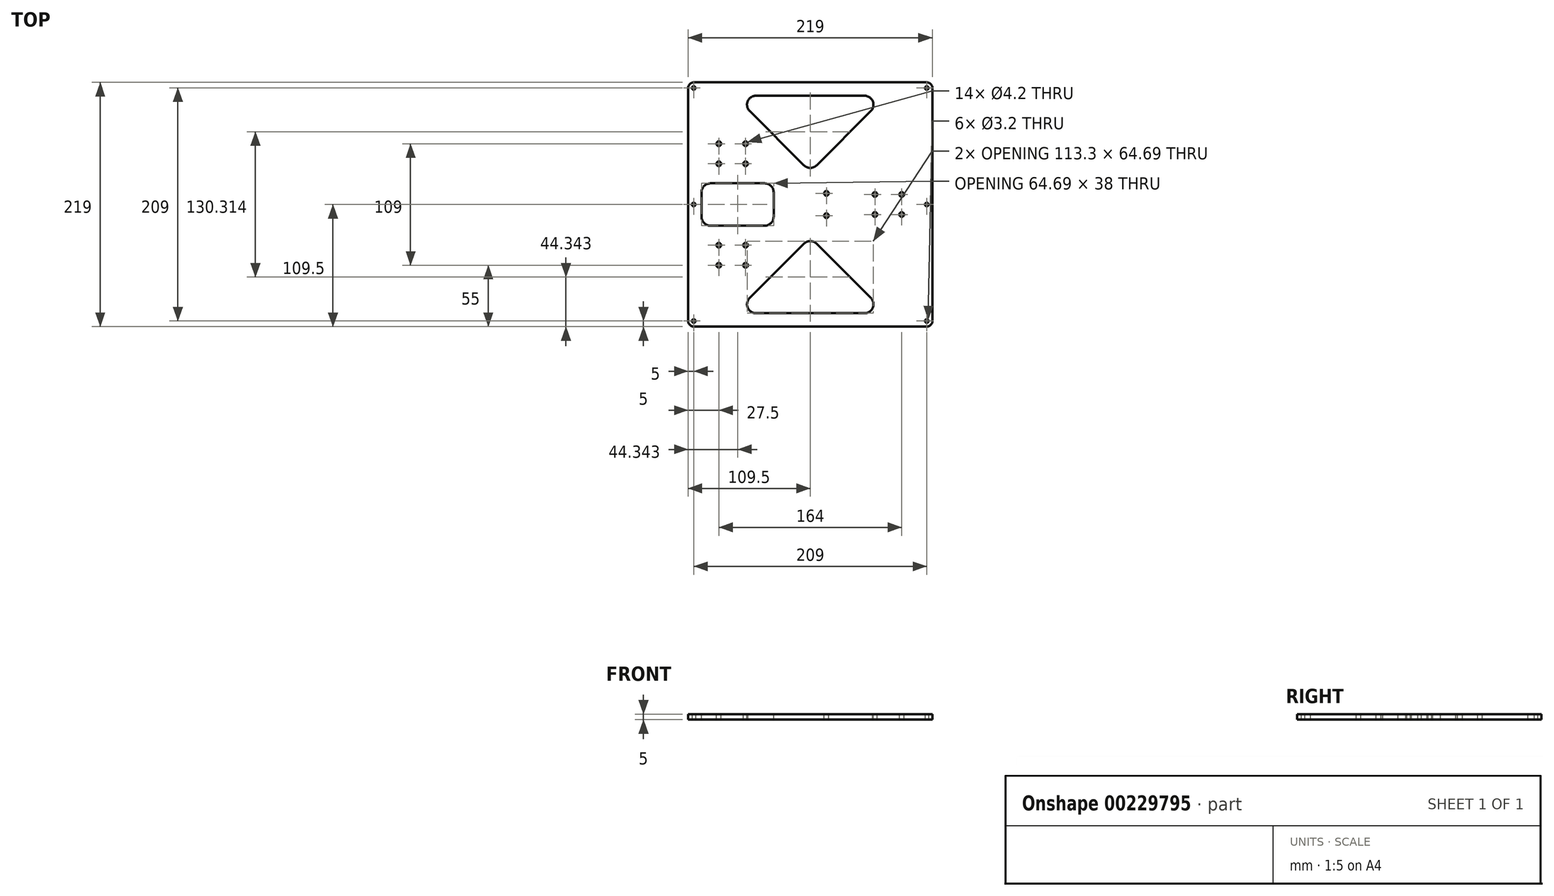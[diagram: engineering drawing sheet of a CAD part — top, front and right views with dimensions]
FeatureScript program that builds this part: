
annotation { "Feature Type Name" : "Feature", "Feature Type Description" : "" }
export const myFeature = defineFeature(function(context is Context, id is Id, definition is map)
    precondition{}
    {
        {
            var Q0;
            Q0=qCreatedBy(makeId("Top.planeOp"),FACE);
            var sketch = newSketch(context, id + "F0", { "sketchPlane" : qUnion([Q0])});
            skLineSegment(sketch, "E0.bottom", {"start": v(109.5, 109.5) * mm, "end": v(-109.5, 109.5) * mm});
            skLineSegment(sketch, "E0.top", {"start": v(109.5, -109.5) * mm, "end": v(-109.5, -109.5) * mm});
            skLineSegment(sketch, "E0.left", {"start": v(109.5, 109.5) * mm, "end": v(109.5, -109.5) * mm});
            skLineSegment(sketch, "E0.right", {"start": v(-109.5, 109.5) * mm, "end": v(-109.5, -109.5) * mm});
            skPoint(sketch, "E0.middle", {"position": v(0, 0) * mm});
            skLineSegment(sketch, "E1.bottom", {"start": v(104.5, 104.5) * mm, "end": v(-104.5, 104.5) * mm, "construction": true});
            skLineSegment(sketch, "E1.top", {"start": v(104.5, -104.5) * mm, "end": v(-104.5, -104.5) * mm, "construction": true});
            skLineSegment(sketch, "E1.left", {"start": v(104.5, 104.5) * mm, "end": v(104.5, -104.5) * mm, "construction": true});
            skLineSegment(sketch, "E1.right", {"start": v(-104.5, 104.5) * mm, "end": v(-104.5, -104.5) * mm, "construction": true});
            skCircle(sketch, "E2", {"center": v(-104.5, 104.5) * mm, "radius": 1.6 * mm});
            skCircle(sketch, "E3", {"center": v(104.5, 104.5) * mm, "radius": 1.6 * mm});
            skCircle(sketch, "E4", {"center": v(104.5, -104.5) * mm, "radius": 1.6 * mm});
            skCircle(sketch, "E5", {"center": v(-104.5, -104.5) * mm, "radius": 1.6 * mm});
            skCircle(sketch, "E6", {"center": v(-104.5, 0) * mm, "radius": 1.6 * mm});
            skCircle(sketch, "E7", {"center": v(104.5, 0) * mm, "radius": 1.6 * mm});
            skSolve(sketch);
        }
        {
            var Q0;
            Q0=makeQuery(id+"F0.imprint","IMPRINT",FACE,{"disambiguationData":[TD([[makeQuery(id+"F0.imprint","IMPRINT",EDGE,{"derivedFrom":sQuery(id+"F0.wireOp",EDGE,"E0.bottom")}),1.0]])]});
            extrude(context, id + "F1", {"entities" : qUnion([Q0]), "depth" : 5 * mm});
        }
        {
            var Q0;
            Q0=makeQuery(id+"F1.opExtrude","CAP_FACE",FACE,{"disambiguationData":[OSD([sQuery(id+"F0.wireOp",EDGE,"E0.bottom"),sQuery(id+"F0.wireOp",EDGE,"E0.top"),sQuery(id+"F0.wireOp",EDGE,"E0.left"),sQuery(id+"F0.wireOp",EDGE,"E0.right"),sQuery(id+"F0.wireOp",EDGE,"E2"),sQuery(id+"F0.wireOp",EDGE,"E3"),sQuery(id+"F0.wireOp",EDGE,"E4"),sQuery(id+"F0.wireOp",EDGE,"E5")])],"isStart":false});
            var sketch = newSketch(context, id + "F2", { "sketchPlane" : qUnion([Q0])});
            skLineSegment(sketch, "E8.bottom", {"start": v(97, 97) * mm, "end": v(-97, 97) * mm, "construction": true});
            skLineSegment(sketch, "E8.top", {"start": v(97, -97) * mm, "end": v(-97, -97) * mm, "construction": true});
            skLineSegment(sketch, "E8.left", {"start": v(97, 97) * mm, "end": v(97, -97) * mm, "construction": true});
            skLineSegment(sketch, "E8.right", {"start": v(-97, 97) * mm, "end": v(-97, -97) * mm, "construction": true});
            skPoint(sketch, "E8.middle", {"position": v(0, 0) * mm});
            skCircle(sketch, "E9", {"center": v(-82, 54.5) * mm, "radius": 2.1 * mm});
            skCircle(sketch, "E10", {"center": v(-82, -36.5) * mm, "radius": 2.1 * mm});
            skCircle(sketch, "E11", {"center": v(-58, -54.5) * mm, "radius": 2.1 * mm});
            skLineSegment(sketch, "E12.bottom", {"start": v(-82, -36.5) * mm, "end": v(-58, -36.5) * mm, "construction": true});
            skLineSegment(sketch, "E12.top", {"start": v(-82, -54.5) * mm, "end": v(-58, -54.5) * mm, "construction": true});
            skLineSegment(sketch, "E12.left", {"start": v(-82, -36.5) * mm, "end": v(-82, -54.5) * mm, "construction": true});
            skLineSegment(sketch, "E12.right", {"start": v(-58, -36.5) * mm, "end": v(-58, -54.5) * mm, "construction": true});
            skLineSegment(sketch, "E13.bottom", {"start": v(-82, 54.5) * mm, "end": v(-58, 54.5) * mm, "construction": true});
            skLineSegment(sketch, "E13.top", {"start": v(-82, 36.5) * mm, "end": v(-58, 36.5) * mm, "construction": true});
            skLineSegment(sketch, "E13.left", {"start": v(-82, 54.5) * mm, "end": v(-82, 36.5) * mm, "construction": true});
            skLineSegment(sketch, "E13.right", {"start": v(-58, 54.5) * mm, "end": v(-58, 36.5) * mm, "construction": true});
            skCircle(sketch, "E14", {"center": v(58, 9) * mm, "radius": 2.1 * mm});
            skLineSegment(sketch, "E15.bottom", {"start": v(58, 9) * mm, "end": v(82, 9) * mm, "construction": true});
            skLineSegment(sketch, "E15.top", {"start": v(58, -9) * mm, "end": v(82, -9) * mm, "construction": true});
            skLineSegment(sketch, "E15.left", {"start": v(58, 9) * mm, "end": v(58, -9) * mm, "construction": true});
            skLineSegment(sketch, "E15.right", {"start": v(82, 9) * mm, "end": v(82, -9) * mm, "construction": true});
            skCircle(sketch, "E16", {"center": v(58, -9) * mm, "radius": 2.1 * mm});
            skCircle(sketch, "E17", {"center": v(82, -9) * mm, "radius": 2.1 * mm});
            skCircle(sketch, "E18", {"center": v(82, 9) * mm, "radius": 2.1 * mm});
            skCircle(sketch, "E19", {"center": v(-82, -54.5) * mm, "radius": 2.1 * mm});
            skCircle(sketch, "E20", {"center": v(-58, 36.5) * mm, "radius": 2.1 * mm});
            skCircle(sketch, "E21", {"center": v(-82, 36.5) * mm, "radius": 2.1 * mm});
            skCircle(sketch, "E22", {"center": v(-58, 54.5) * mm, "radius": 2.1 * mm});
            skCircle(sketch, "E23", {"center": v(-58, -36.5) * mm, "radius": 2.1 * mm});
            skCircle(sketch, "E24", {"center": v(14.5, 10) * mm, "radius": 2.1 * mm});
            skCircle(sketch, "E25", {"center": v(14.5, -10) * mm, "radius": 2.1 * mm});
            skLineSegment(sketch, "E26", {"start": v(14.5, 10) * mm, "end": v(14.5, -10) * mm, "construction": true});
            skLineSegment(sketch, "E27", {"start": v(-104.5, 104.5) * mm, "end": v(104.5, 104.5) * mm, "construction": true});
            skLineSegment(sketch, "E28", {"start": v(-104.5, -104.5) * mm, "end": v(104.5, -104.5) * mm, "construction": true});
            skSolve(sketch);
        }
        {
            var Q0;
            Q0=makeQuery(id+"F2.imprint","IMPRINT",FACE,{"disambiguationData":[TD([[makeQuery(id+"F2.imprint","IMPRINT",EDGE,{"derivedFrom":sQuery(id+"F2.wireOp",EDGE,"E19")}),1.0]])]});
            var Q1;
            Q1=makeQuery(id+"F2.imprint","IMPRINT",FACE,{"disambiguationData":[TD([[makeQuery(id+"F2.imprint","IMPRINT",EDGE,{"derivedFrom":sQuery(id+"F2.wireOp",EDGE,"E11")}),1.0]])]});
            var Q2;
            Q2=makeQuery(id+"F2.imprint","IMPRINT",FACE,{"disambiguationData":[TD([[makeQuery(id+"F2.imprint","IMPRINT",EDGE,{"derivedFrom":sQuery(id+"F2.wireOp",EDGE,"E23")}),1.0]])]});
            var Q3;
            Q3=makeQuery(id+"F2.imprint","IMPRINT",FACE,{"disambiguationData":[TD([[makeQuery(id+"F2.imprint","IMPRINT",EDGE,{"derivedFrom":sQuery(id+"F2.wireOp",EDGE,"E10")}),1.0]])]});
            var Q4;
            Q4=makeQuery(id+"F2.imprint","IMPRINT",FACE,{"disambiguationData":[TD([[makeQuery(id+"F2.imprint","IMPRINT",EDGE,{"derivedFrom":sQuery(id+"F2.wireOp",EDGE,"E21")}),1.0]])]});
            var Q5;
            Q5=makeQuery(id+"F2.imprint","IMPRINT",FACE,{"disambiguationData":[TD([[makeQuery(id+"F2.imprint","IMPRINT",EDGE,{"derivedFrom":sQuery(id+"F2.wireOp",EDGE,"E9")}),1.0]])]});
            var Q6;
            Q6=makeQuery(id+"F2.imprint","IMPRINT",FACE,{"disambiguationData":[TD([[makeQuery(id+"F2.imprint","IMPRINT",EDGE,{"derivedFrom":sQuery(id+"F2.wireOp",EDGE,"E22")}),1.0]])]});
            var Q7;
            Q7=makeQuery(id+"F2.imprint","IMPRINT",FACE,{"disambiguationData":[TD([[makeQuery(id+"F2.imprint","IMPRINT",EDGE,{"derivedFrom":sQuery(id+"F2.wireOp",EDGE,"E20")}),1.0]])]});
            var Q8;
            Q8=makeQuery(id+"F2.imprint","IMPRINT",FACE,{"disambiguationData":[TD([[makeQuery(id+"F2.imprint","IMPRINT",EDGE,{"derivedFrom":sQuery(id+"F2.wireOp",EDGE,"E25")}),1.0]])]});
            var Q9;
            Q9=makeQuery(id+"F2.imprint","IMPRINT",FACE,{"disambiguationData":[TD([[makeQuery(id+"F2.imprint","IMPRINT",EDGE,{"derivedFrom":sQuery(id+"F2.wireOp",EDGE,"E16")}),1.0]])]});
            var Q10;
            Q10=makeQuery(id+"F2.imprint","IMPRINT",FACE,{"disambiguationData":[TD([[makeQuery(id+"F2.imprint","IMPRINT",EDGE,{"derivedFrom":sQuery(id+"F2.wireOp",EDGE,"E17")}),1.0]])]});
            var Q11;
            Q11=makeQuery(id+"F2.imprint","IMPRINT",FACE,{"disambiguationData":[TD([[makeQuery(id+"F2.imprint","IMPRINT",EDGE,{"derivedFrom":sQuery(id+"F2.wireOp",EDGE,"E18")}),1.0]])]});
            var Q12;
            Q12=makeQuery(id+"F2.imprint","IMPRINT",FACE,{"disambiguationData":[TD([[makeQuery(id+"F2.imprint","IMPRINT",EDGE,{"derivedFrom":sQuery(id+"F2.wireOp",EDGE,"E14")}),1.0]])]});
            var Q13;
            Q13=makeQuery(id+"F2.imprint","IMPRINT",FACE,{"disambiguationData":[TD([[makeQuery(id+"F2.imprint","IMPRINT",EDGE,{"derivedFrom":sQuery(id+"F2.wireOp",EDGE,"E24")}),1.0]])]});
            var Q14;
            Q14=sQuery(id+"F2.wireOp",EDGE,"E21");
            var Q15;
            Q15=sQuery(id+"F2.wireOp",EDGE,"E9");
            var Q16;
            Q16=sQuery(id+"F2.wireOp",EDGE,"E22");
            var Q17;
            Q17=sQuery(id+"F2.wireOp",EDGE,"E20");
            var Q18;
            Q18=sQuery(id+"F2.wireOp",EDGE,"E23");
            var Q19;
            Q19=sQuery(id+"F2.wireOp",EDGE,"E11");
            var Q20;
            Q20=sQuery(id+"F2.wireOp",EDGE,"E19");
            var Q21;
            Q21=sQuery(id+"F2.wireOp",EDGE,"E10");
            var Q22;
            Q22=sQuery(id+"F2.wireOp",EDGE,"E24");
            var Q23;
            Q23=sQuery(id+"F2.wireOp",EDGE,"E25");
            var Q24;
            Q24=sQuery(id+"F2.wireOp",EDGE,"E14");
            var Q25;
            Q25=sQuery(id+"F2.wireOp",EDGE,"E16");
            var Q26;
            Q26=sQuery(id+"F2.wireOp",EDGE,"E17");
            var Q27;
            Q27=sQuery(id+"F2.wireOp",EDGE,"E18");
            extrude(context, id + "F3", {"entities" : qUnion([Q0, Q1, Q2, Q3, Q4, Q5, Q6, Q7, Q8, Q9, Q10, Q11, Q12, Q13]), "operationType" : NewBodyOperationType.REMOVE, "surfaceEntities" : qUnion([Q14, Q15, Q16, Q17, Q18, Q19, Q20, Q21, Q22, Q23, Q24, Q25, Q26, Q27]), "oppositeDirection" : true, "depth" : 25 * mm});
        }
        {
            var Q0;
            Q0=makeQuery(id+"F1.opExtrude","SWEPT_EDGE",EDGE,{"disambiguationData":[OSD([sQuery(id+"F0.wireOp",EDGE,"E0.bottom"),sQuery(id+"F0.wireOp",EDGE,"E0.left")])]});
            var Q1;
            Q1=makeQuery(id+"F1.opExtrude","SWEPT_EDGE",EDGE,{"disambiguationData":[OSD([sQuery(id+"F0.wireOp",EDGE,"E0.top"),sQuery(id+"F0.wireOp",EDGE,"E0.left")])]});
            var Q2;
            Q2=makeQuery(id+"F1.opExtrude","SWEPT_EDGE",EDGE,{"disambiguationData":[OSD([sQuery(id+"F0.wireOp",EDGE,"E0.top"),sQuery(id+"F0.wireOp",EDGE,"E0.right")])]});
            var Q3;
            Q3=makeQuery(id+"F1.opExtrude","SWEPT_EDGE",EDGE,{"disambiguationData":[OSD([sQuery(id+"F0.wireOp",EDGE,"E0.bottom"),sQuery(id+"F0.wireOp",EDGE,"E0.right")])]});
            fillet(context, id + "F4", {"entities" : qUnion([Q0, Q1, Q2, Q3]), "radius" : 5 * mm, "tangentPropagation" : true, "allowEdgeOverflow" : false});
        }
        {
            var Q0;
            Q0=makeQuery(id+"F1.opExtrude","CAP_FACE",FACE,{"disambiguationData":[OSD([sQuery(id+"F0.wireOp",EDGE,"E0.bottom"),sQuery(id+"F0.wireOp",EDGE,"E0.top"),sQuery(id+"F0.wireOp",EDGE,"E0.left"),sQuery(id+"F0.wireOp",EDGE,"E0.right"),sQuery(id+"F0.wireOp",EDGE,"E2"),sQuery(id+"F0.wireOp",EDGE,"E3"),sQuery(id+"F0.wireOp",EDGE,"E4"),sQuery(id+"F0.wireOp",EDGE,"E5")])],"isStart":false});
            var sketch = newSketch(context, id + "F5", { "sketchPlane" : qUnion([Q0])});
            skLineSegment(sketch, "E29", {"start": v(-54.34, -83.84) * mm, "end": v(-5.66, -35.16) * mm});
            skLineSegment(sketch, "E30", {"start": v(5.66, -35.16) * mm, "end": v(54.34, -83.84) * mm});
            skLineSegment(sketch, "E31", {"start": v(54.34, 83.84) * mm, "end": v(5.66, 35.16) * mm});
            skLineSegment(sketch, "E32", {"start": v(-5.66, 35.16) * mm, "end": v(-54.34, 83.84) * mm});
            skLineSegment(sketch, "E33", {"start": v(-48.69, -97.5) * mm, "end": v(48.69, -97.5) * mm});
            skPoint(sketch, "E34.visualSharp", {"position": v(0, -29.5) * mm});
            skArc(sketch, "E34.filletArc", {"start": v(5.66, -35.16) * mm, "mid": v(0, -32.81) * mm, "end": v(-5.66, -35.16) * mm});
            skLineSegment(sketch, "E35", {"start": v(-48.69, 97.5) * mm, "end": v(48.69, 97.5) * mm});
            skPoint(sketch, "E36.visualSharp", {"position": v(0, 29.5) * mm});
            skArc(sketch, "E36.filletArc", {"start": v(-5.66, 35.16) * mm, "mid": v(0, 32.81) * mm, "end": v(5.66, 35.16) * mm});
            skPoint(sketch, "E37.newPointB", {"position": v(94.5, -124) * mm});
            skArc(sketch, "E37.filletArc", {"start": v(48.69, -97.5) * mm, "mid": v(56.08, -92.56) * mm, "end": v(54.34, -83.84) * mm});
            skPoint(sketch, "E38.newPointB", {"position": v(-94.5, -124) * mm});
            skArc(sketch, "E38.filletArc", {"start": v(-54.34, -83.84) * mm, "mid": v(-56.08, -92.56) * mm, "end": v(-48.69, -97.5) * mm});
            skPoint(sketch, "E39.newPointA", {"position": v(-94.5, 124) * mm});
            skArc(sketch, "E39.filletArc", {"start": v(-48.69, 97.5) * mm, "mid": v(-56.08, 92.56) * mm, "end": v(-54.34, 83.84) * mm});
            skPoint(sketch, "E40.newPointB", {"position": v(94.5, 124) * mm});
            skArc(sketch, "E40.filletArc", {"start": v(54.34, 83.84) * mm, "mid": v(56.08, 92.56) * mm, "end": v(48.69, 97.5) * mm});
            skLineSegment(sketch, "E41.bottom", {"start": v(-40.81, -19) * mm, "end": v(-89.5, -19) * mm});
            skLineSegment(sketch, "E41.top", {"start": v(-40.81, 19) * mm, "end": v(-89.5, 19) * mm});
            skLineSegment(sketch, "E41.left", {"start": v(-32.81, -11) * mm, "end": v(-32.81, 11) * mm});
            skLineSegment(sketch, "E41.right", {"start": v(-97.5, -11) * mm, "end": v(-97.5, 11) * mm});
            skPoint(sketch, "E41.middle", {"position": v(-65.16, 0) * mm});
            skPoint(sketch, "E42.visualSharp", {"position": v(-97.5, 19) * mm});
            skArc(sketch, "E42.filletArc", {"start": v(-89.5, 19) * mm, "mid": v(-95.16, 16.66) * mm, "end": v(-97.5, 11) * mm});
            skPoint(sketch, "E43.visualSharp", {"position": v(-32.81, 19) * mm});
            skArc(sketch, "E43.filletArc", {"start": v(-32.81, 11) * mm, "mid": v(-35.16, 16.66) * mm, "end": v(-40.81, 19) * mm});
            skPoint(sketch, "E44.visualSharp", {"position": v(-32.81, -19) * mm});
            skArc(sketch, "E44.filletArc", {"start": v(-40.81, -19) * mm, "mid": v(-35.16, -16.66) * mm, "end": v(-32.81, -11) * mm});
            skPoint(sketch, "E45.visualSharp", {"position": v(-97.5, -19) * mm});
            skArc(sketch, "E45.filletArc", {"start": v(-97.5, -11) * mm, "mid": v(-95.16, -16.66) * mm, "end": v(-89.5, -19) * mm});
            skSolve(sketch);
        }
        {
            var Q0;
            {var subQ2=sQuery(id+"F5.wireOp",EDGE,"E33");Q0=makeQuery(id+"F5.imprint","IMPRINT",FACE,{"disambiguationData":[TD([[makeQuery(id+"F5.imprint","IMPRINT",EDGE,{"derivedFrom":subQ2}),1.0]])]});}
            var Q1;
            {var subQ2=sQuery(id+"F5.wireOp",EDGE,"E35");Q1=makeQuery(id+"F5.imprint","IMPRINT",FACE,{"disambiguationData":[TD([[makeQuery(id+"F5.imprint","IMPRINT",EDGE,{"derivedFrom":subQ2}),-1.0]])]});}
            var Q2;
            Q2=makeQuery(id+"F5.imprint","IMPRINT",FACE,{"disambiguationData":[TD([[makeQuery(id+"F5.imprint","IMPRINT",EDGE,{"derivedFrom":sQuery(id+"F5.wireOp",EDGE,"E41.bottom")}),-1.0]])]});
            extrude(context, id + "F6", {"entities" : qUnion([Q0, Q1, Q2]), "operationType" : NewBodyOperationType.REMOVE, "oppositeDirection" : true, "depth" : 25 * mm});
        }
    });
